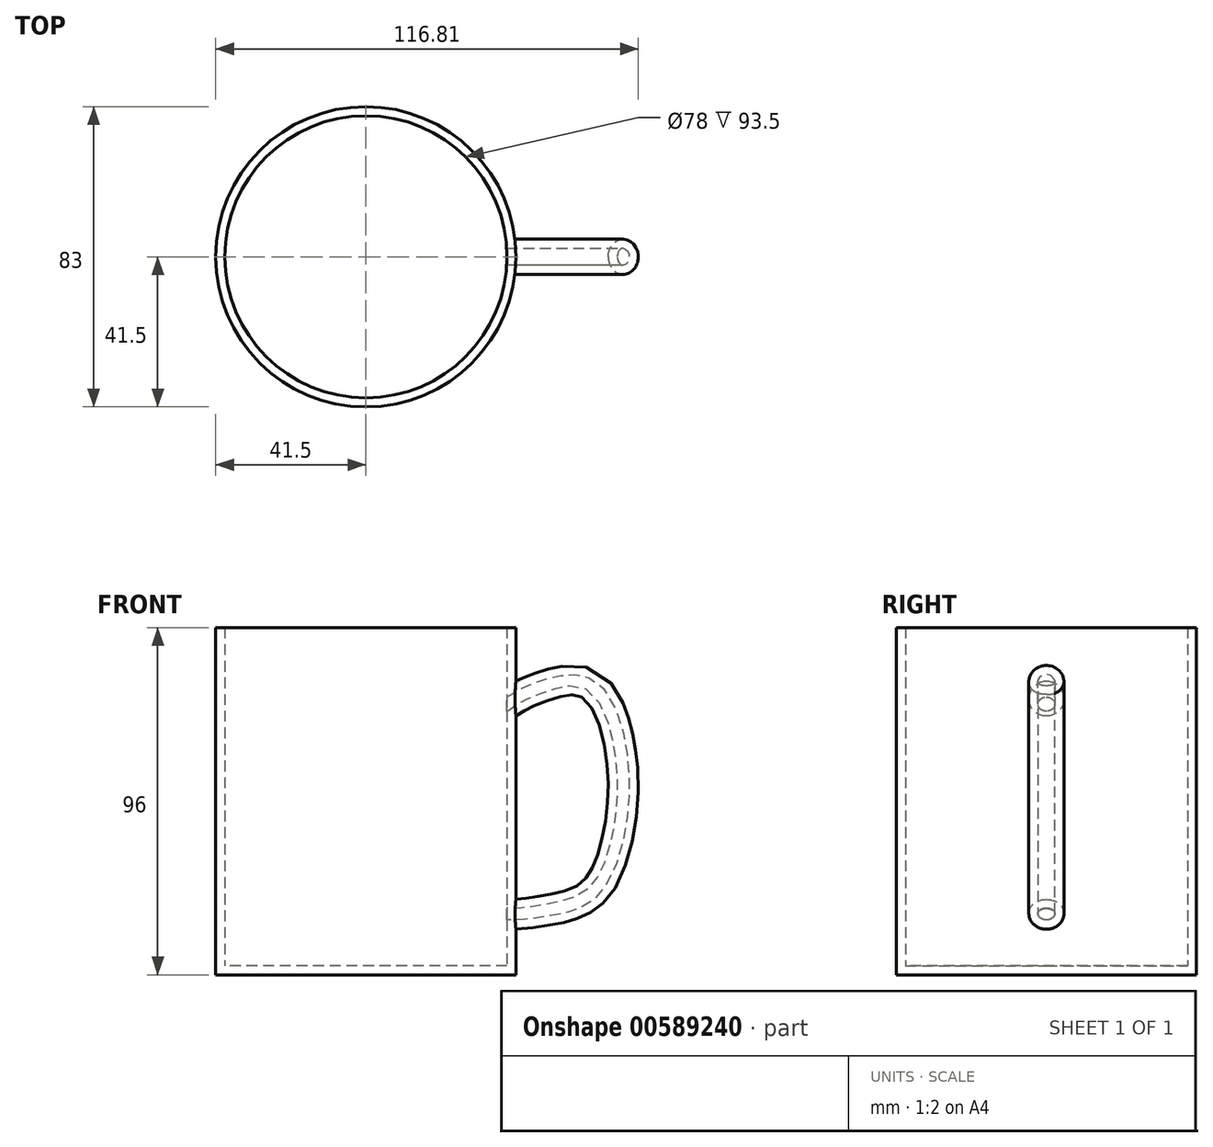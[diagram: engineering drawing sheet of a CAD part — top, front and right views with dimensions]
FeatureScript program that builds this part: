
annotation { "Feature Type Name" : "Feature", "Feature Type Description" : "" }
export const myFeature = defineFeature(function(context is Context, id is Id, definition is map)
    precondition{}
    {
        {
            var Q0;
            Q0=qCreatedBy(makeId("Top.planeOp"),FACE);
            var sketch = newSketch(context, id + "F0", { "sketchPlane" : qUnion([Q0])});
            skCircle(sketch, "E0", {"center": v(0, 0) * mm, "radius": 41.5 * mm});
            skSolve(sketch);
        }
        {
            var Q0;
            Q0=makeQuery(id+"F0.imprint","IMPRINT",FACE,{"disambiguationData":[TD([[makeQuery(id+"F0.imprint","IMPRINT",EDGE,{"derivedFrom":sQuery(id+"F0.wireOp",EDGE,"E0")}),1.0]])]});
            extrude(context, id + "F1", {"entities" : qUnion([Q0]), "depth" : 96 * mm, "offsetDistance" : 25 * mm});
        }
        {
            var Q0;
            Q0=qCreatedBy(makeId("Right.planeOp"),FACE);
            cPlane(context, id + "F2", {"entities" : qUnion([Q0]), "cplaneType" : CPlaneType.OFFSET, "offset" : 41.5 * mm, "width" : 150 * mm, "height" : 150 * mm});
        }
        {
            var Q0;
            Q0=qCreatedBy(makeId("Front.planeOp"),FACE);
            var sketch = newSketch(context, id + "F3", { "sketchPlane" : qUnion([Q0])});
            skFitSpline(sketch, "E1", {"points": [v(36.9, 72.97) * mm, v(46.39, 78.31) * mm, v(60.74, 80.03) * mm, v(69.96, 61.82) * mm, v(69.1, 37.82) * mm, v(61.6, 22.6) * mm, v(49.04, 18.13) * mm, v(39.2, 17.37) * mm, v(29.4, 19.84) * mm], "startDerivative": vector(145.05, 94.36) * mm, "endDerivative": vector(-117.92, 32.4) * mm});
            skSolve(sketch);
        }
        {
            var Q0;
            Q0=qCreatedBy(id+"F2.planeOp",FACE);
            var sketch = newSketch(context, id + "F4", { "sketchPlane" : qUnion([Q0])});
            skCircle(sketch, "E2", {"center": v(0, 76.38) * mm, "radius": 4.84 * mm});
            skSolve(sketch);
        }
        {
            var Q0;
            Q0=makeQuery(id+"F4.imprint","IMPRINT",FACE,{"disambiguationData":[TD([[makeQuery(id+"F4.imprint","IMPRINT",EDGE,{"derivedFrom":sQuery(id+"F4.wireOp",EDGE,"E2")}),1.0]])]});
            var Q1;
            Q1=sQuery(id+"F3.wireOp",EDGE,"E1");
            sweep(context, id + "F5", {"operationType" : NewBodyOperationType.ADD, "profiles" : qUnion([Q0]), "path" : qUnion([Q1])});
        }
        {
            var Q0;
            Q0=makeQuery(id+"F1.opExtrude","CAP_FACE",FACE,{"disambiguationData":[OSD([sQuery(id+"F0.wireOp",EDGE,"E0")])],"isStart":false});
            shell(context, id + "F6", {"entities" : qUnion([Q0]), "thickness" : 2.5 * mm});
        }
    });
